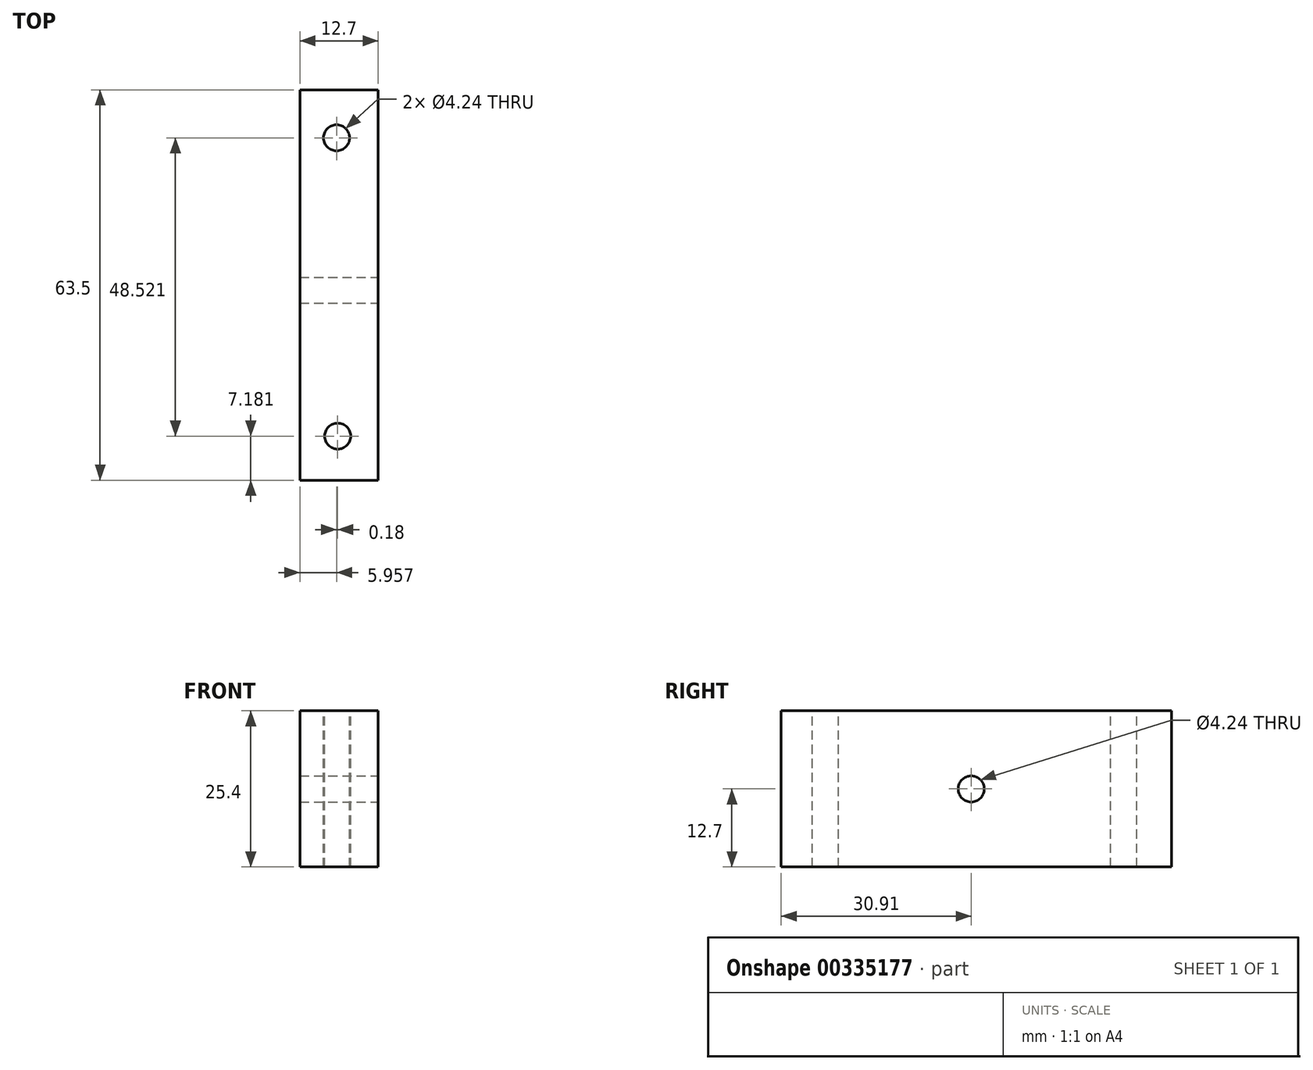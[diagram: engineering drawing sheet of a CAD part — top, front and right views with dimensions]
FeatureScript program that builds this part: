
annotation { "Feature Type Name" : "Feature", "Feature Type Description" : "" }
export const myFeature = defineFeature(function(context is Context, id is Id, definition is map)
    precondition{}
    {
        {
            var Q0;
            Q0=qCreatedBy(makeId("Right.planeOp"),FACE);
            var sketch = newSketch(context, id + "F0", { "sketchPlane" : qUnion([Q0])});
            skLineSegment(sketch, "E0.bottom", {"start": v(-30.9, 0) * mm, "end": v(32.6, 0) * mm});
            skLineSegment(sketch, "E0.top", {"start": v(-30.9, -25.4) * mm, "end": v(32.6, -25.4) * mm});
            skLineSegment(sketch, "E0.left", {"start": v(-30.9, 0) * mm, "end": v(-30.9, -25.4) * mm});
            skLineSegment(sketch, "E0.right", {"start": v(32.6, 0) * mm, "end": v(32.6, -25.4) * mm});
            skSolve(sketch);
        }
        {
            var Q0;
            Q0=qSketchRegion(id+"F0",true);
            extrude(context, id + "F1", {"entities" : qUnion([Q0]), "depth" : 12.7 * mm});
        }
        {
            var Q0;
            {var subQ0=sQuery(id+"F0.wireOp",EDGE,"E0.bottom");Q0=makeQuery(id+"F1.opExtrude","SWEPT_FACE",FACE,{"disambiguationData":[OSD([subQ0]),TDD([makeQuery(id+"F0.imprint","IMPRINT",EDGE,{"disambiguationData":[TD([[makeQuery(id+"F0.imprint","INTERSECT",VERTEX,{"derivedFrom":[subQ0,sQuery(id+"F0.wireOp",EDGE,"E0.left")]}),-1.0]])],"derivedFrom":subQ0})])]});}
            var sketch = newSketch(context, id + "F2", { "sketchPlane" : qUnion([Q0])});
            skCircle(sketch, "E1", {"center": v(5.96, 24.8) * mm, "radius": 2.12 * mm});
            skSolve(sketch);
        }
        {
            var Q0;
            Q0=qSketchRegion(id+"F2",true);
            extrude(context, id + "F3", {"entities" : qUnion([Q0]), "operationType" : NewBodyOperationType.REMOVE, "oppositeDirection" : true, "depth" : 25.4 * mm});
        }
        {
            var Q0;
            {var subQ0=sQuery(id+"F0.wireOp",EDGE,"E0.bottom");Q0=makeQuery(id+"F1.opExtrude","SWEPT_FACE",FACE,{"disambiguationData":[OSD([subQ0]),TDD([makeQuery(id+"F0.imprint","IMPRINT",EDGE,{"disambiguationData":[TD([[makeQuery(id+"F0.imprint","INTERSECT",VERTEX,{"derivedFrom":[subQ0,sQuery(id+"F0.wireOp",EDGE,"E0.left")]}),-1.0]])],"derivedFrom":subQ0})])]});}
            var sketch = newSketch(context, id + "F4", { "sketchPlane" : qUnion([Q0])});
            skCircle(sketch, "E2", {"center": v(6.14, -23.73) * mm, "radius": 2.12 * mm});
            skSolve(sketch);
        }
        {
            var Q0;
            Q0=qSketchRegion(id+"F4",true);
            extrude(context, id + "F5", {"entities" : qUnion([Q0]), "operationType" : NewBodyOperationType.REMOVE, "oppositeDirection" : true, "depth" : 25.4 * mm});
        }
        {
            var Q0;
            Q0=makeQuery(id+"F1.opExtrude","CAP_FACE",FACE,{"disambiguationData":[OSD([sQuery(id+"F0.wireOp",EDGE,"E0.bottom"),sQuery(id+"F0.wireOp",EDGE,"E0.top"),sQuery(id+"F0.wireOp",EDGE,"E0.left"),sQuery(id+"F0.wireOp",EDGE,"E0.right")])],"isStart":false});
            var sketch = newSketch(context, id + "F6", { "sketchPlane" : qUnion([Q0])});
            skCircle(sketch, "E3", {"center": v(0, -12.7) * mm, "radius": 2.12 * mm});
            skSolve(sketch);
        }
        {
            var Q0;
            Q0 = qSketchRegion(id + "F6", true);
            extrude(context, id + "F7", {"entities" : qUnion([Q0]), "operationType" : NewBodyOperationType.REMOVE, "oppositeDirection" : true, "depth" : 25.4 * mm});
        }
    });
